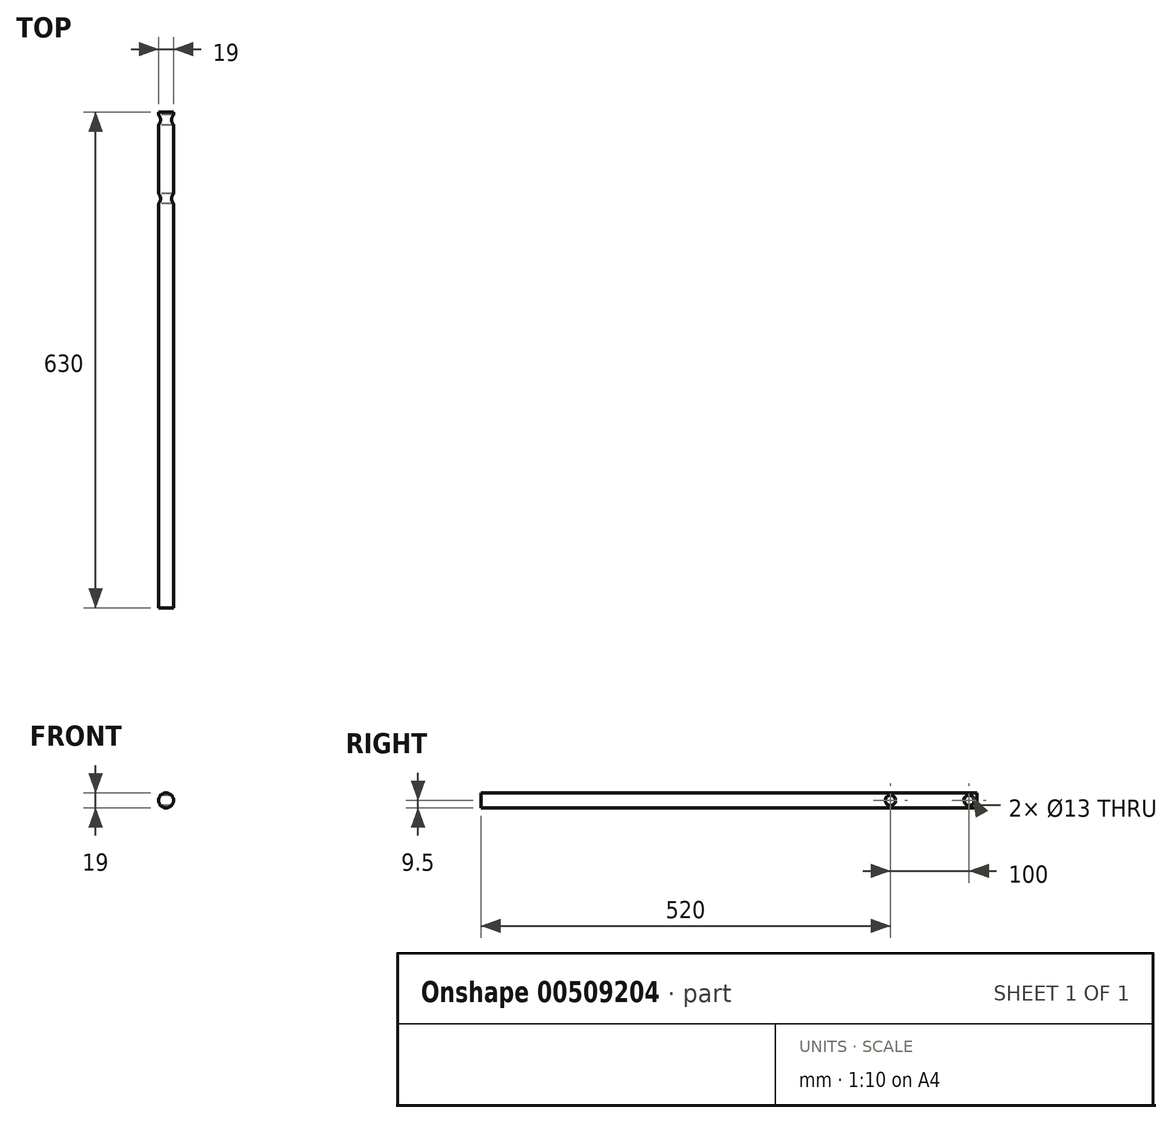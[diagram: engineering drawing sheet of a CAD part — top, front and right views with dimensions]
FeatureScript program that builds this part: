
annotation { "Feature Type Name" : "Feature", "Feature Type Description" : "" }
export const myFeature = defineFeature(function(context is Context, id is Id, definition is map)
    precondition{}
    {
        {
            var Q0;
            Q0=qCreatedBy(makeId("Front.planeOp"),FACE);
            var sketch = newSketch(context, id + "F0", { "sketchPlane" : qUnion([Q0])});
            skCircle(sketch, "E0", {"center": v(0, 0) * mm, "radius": 9.5 * mm});
            skSolve(sketch);
        }
        {
            var Q0;
            Q0 = qSketchRegion(id + "F0", true);
            extrude(context, id + "F1", {"entities" : qUnion([Q0]), "depth" : 630 * mm});
        }
        {
            var Q0;
            Q0=qCreatedBy(makeId("Right.planeOp"),FACE);
            var sketch = newSketch(context, id + "F2", { "sketchPlane" : qUnion([Q0])});
            skCircle(sketch, "E1", {"center": v(-10, 0) * mm, "radius": 6.5 * mm});
            skCircle(sketch, "E2", {"center": v(-110, 0) * mm, "radius": 6.5 * mm});
            skSolve(sketch);
        }
        {
            var Q0;
            Q0 = qSketchRegion(id + "F2", true);
            extrude(context, id + "F3", {"entities" : qUnion([Q0]), "operationType" : NewBodyOperationType.REMOVE, "depth" : 25 * mm, "hasSecondDirection" : true, "secondDirectionOppositeDirection" : true, "secondDirectionDepth" : 25 * mm});
        }
    });
